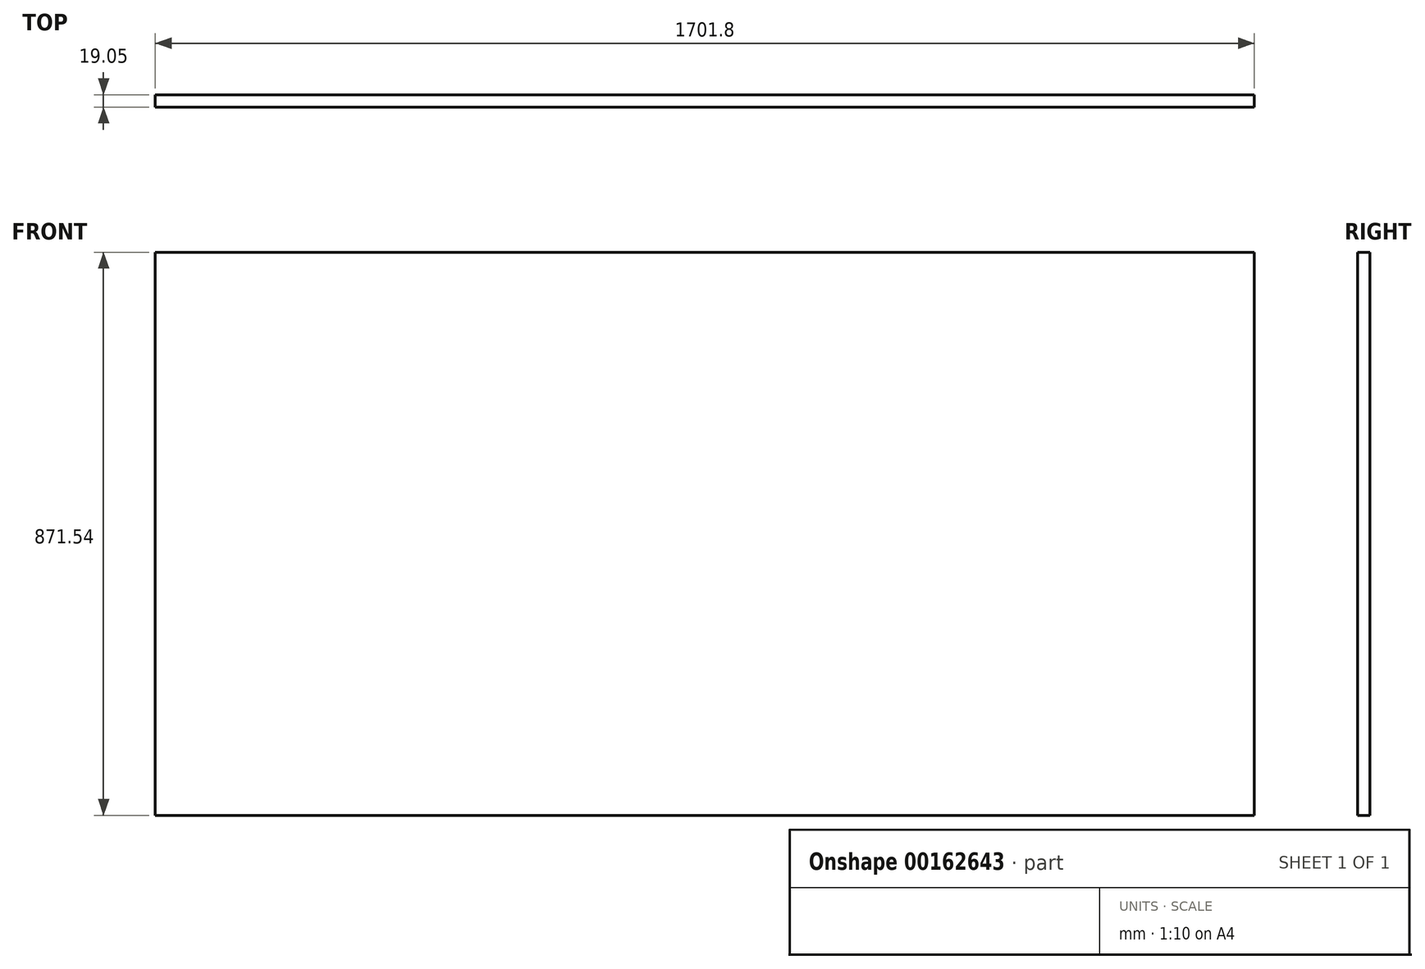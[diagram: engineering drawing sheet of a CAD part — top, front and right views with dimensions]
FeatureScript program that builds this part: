
annotation { "Feature Type Name" : "Feature", "Feature Type Description" : "" }
export const myFeature = defineFeature(function(context is Context, id is Id, definition is map)
    precondition{}
    {
        {
            var Q0;
            Q0=qCreatedBy(makeId("Front.planeOp"),FACE);
            var sketch = newSketch(context, id + "F0", { "sketchPlane" : qUnion([Q0])});
            skLineSegment(sketch, "E0.bottom", {"start": v(-837.26, 440.87) * mm, "end": v(864.54, 440.87) * mm});
            skLineSegment(sketch, "E0.top", {"start": v(-837.26, -430.67) * mm, "end": v(864.54, -430.67) * mm});
            skLineSegment(sketch, "E0.left", {"start": v(-837.26, 440.87) * mm, "end": v(-837.26, -430.67) * mm});
            skLineSegment(sketch, "E0.right", {"start": v(864.54, 440.87) * mm, "end": v(864.54, -430.67) * mm});
            skSolve(sketch);
        }
        {
            var Q0;
            Q0 = qSketchRegion(id + "F0", true);
            extrude(context, id + "F1", {"entities" : qUnion([Q0]), "depth" : 19.05 * mm});
        }
    });
